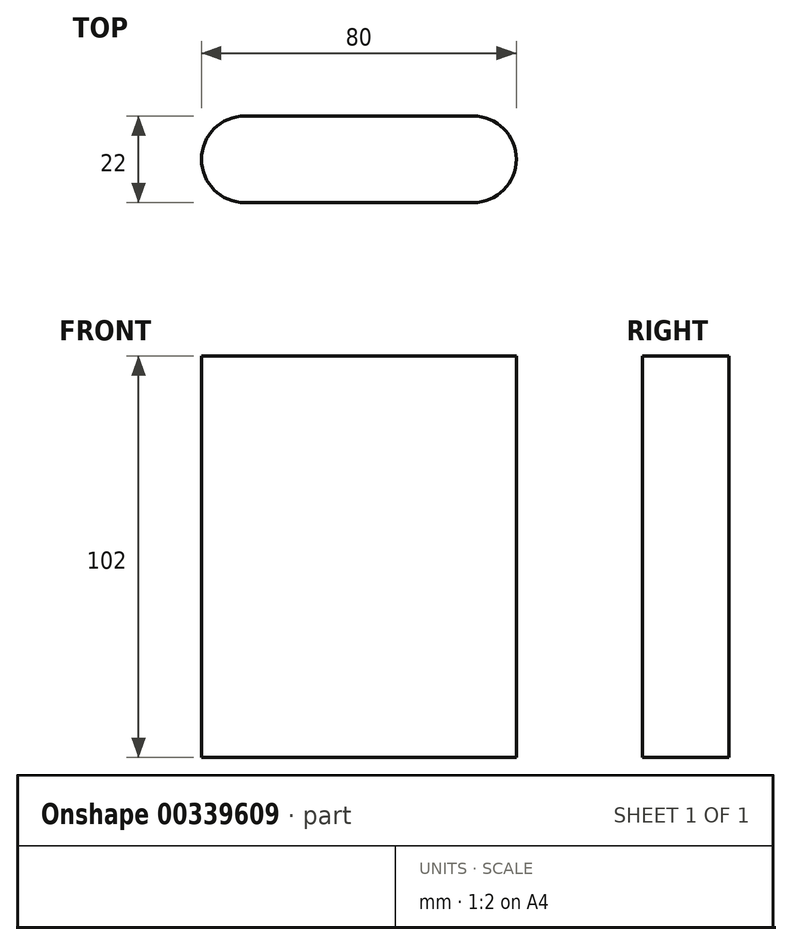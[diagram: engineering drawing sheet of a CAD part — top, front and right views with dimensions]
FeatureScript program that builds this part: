
annotation { "Feature Type Name" : "Feature", "Feature Type Description" : "" }
export const myFeature = defineFeature(function(context is Context, id is Id, definition is map)
    precondition{}
    {
        {
            var Q0;
            Q0=qCreatedBy(makeId("Top.planeOp"),FACE);
            var sketch = newSketch(context, id + "F0", { "sketchPlane" : qUnion([Q0])});
            skLineSegment(sketch, "E0.bottom", {"start": v(-29, 11) * mm, "end": v(29, 11) * mm});
            skLineSegment(sketch, "E0.top", {"start": v(-29, -11) * mm, "end": v(29, -11) * mm});
            skLineSegment(sketch, "E0.left", {"start": v(-29, 11) * mm, "end": v(-29, -11) * mm});
            skLineSegment(sketch, "E0.right", {"start": v(29, 11) * mm, "end": v(29, -11) * mm});
            skLineSegment(sketch, "E1", {"start": v(-29, 0) * mm, "end": v(29, 0) * mm});
            skPoint(sketch, "E2", {"position": v(0, 0) * mm});
            skCircle(sketch, "E3", {"center": v(-29, 0) * mm, "radius": 11 * mm});
            skCircle(sketch, "E4", {"center": v(29, 0) * mm, "radius": 11 * mm});
            skSolve(sketch);
        }
        {
            var Q0;
            Q0=qSketchRegion(id+"F0",true);
            extrude(context, id + "F1", {"entities" : qUnion([Q0]), "endBound" : BoundingType.SYMMETRIC, "depth" : 102 * mm});
        }
    });
